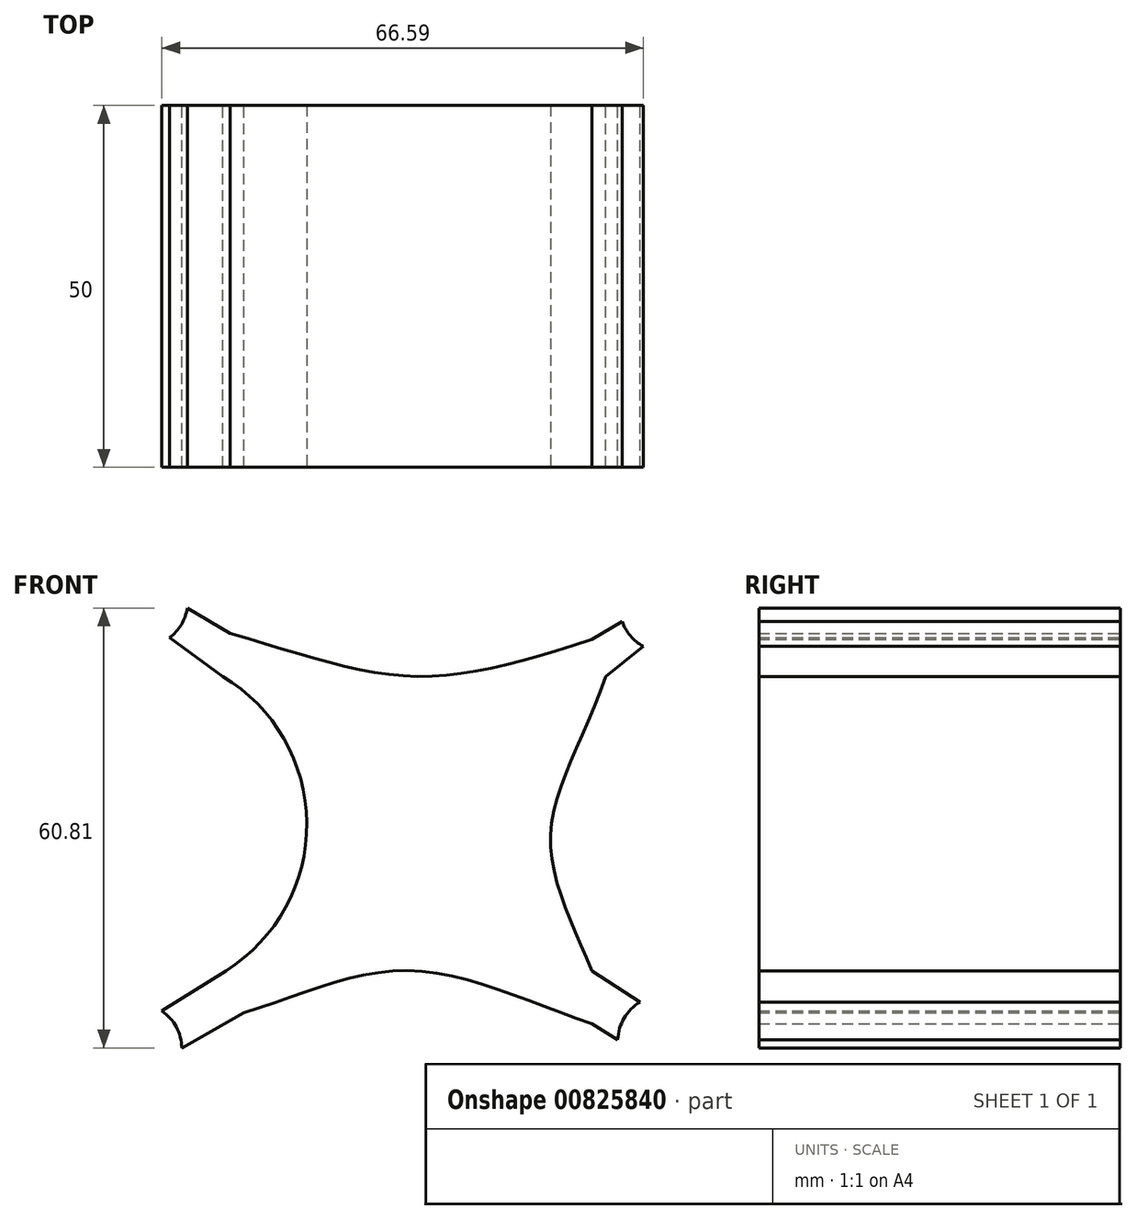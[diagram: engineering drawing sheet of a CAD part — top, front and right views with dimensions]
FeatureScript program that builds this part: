
annotation { "Feature Type Name" : "Feature", "Feature Type Description" : "" }
export const myFeature = defineFeature(function(context is Context, id is Id, definition is map)
    precondition{}
    {
        {
            var Q0;
            Q0=qCreatedBy(makeId("Front.planeOp"),FACE);
            var sketch = newSketch(context, id + "F0", { "sketchPlane" : qUnion([Q0])});
            skFitSpline(sketch, "E0", {"points": [v(-24.9, 27.81) * mm, v(0, 21.88) * mm, v(25.14, 27) * mm], "startDerivative": vector(57.8, -16.86) * mm, "endDerivative": vector(59.8, 19.27) * mm});
            skFitSpline(sketch, "E1", {"points": [v(-23.03, -24.68) * mm, v(0, -18.82) * mm, v(25.14, -26.2) * mm], "startDerivative": vector(50.66, 15.76) * mm, "endDerivative": vector(51.2, -17.15) * mm});
            skFitSpline(sketch, "E2", {"points": [v(-25.96, 21.84) * mm, v(-19.9, 0) * mm, v(-25.5, -18.86) * mm], "startDerivative": vector(18.38, -48.38) * mm, "endDerivative": vector(-20.64, -43.87) * mm});
            skFitSpline(sketch, "E3", {"points": [v(27, 21.84) * mm, v(19.4, 0) * mm, v(25.14, -18.86) * mm], "startDerivative": vector(-16.97, -49.86) * mm, "endDerivative": vector(17.53, -41.49) * mm});
            skCircle(sketch, "E4", {"center": v(35.05, -28.62) * mm, "radius": 6.35 * mm});
            skCircle(sketch, "E5", {"center": v(35.2, 31.51) * mm, "radius": 6.25 * mm});
            skLineSegment(sketch, "E6", {"start": v(-25.96, 21.84) * mm, "end": v(-35.41, 28.75) * mm});
            skLineSegment(sketch, "E7", {"start": v(-24.9, 27.81) * mm, "end": v(-32.52, 32.27) * mm});
            skLineSegment(sketch, "E8", {"start": v(25.14, -26.2) * mm, "end": v(32.16, -30.54) * mm});
            skLineSegment(sketch, "E9", {"start": v(35.81, -25.82) * mm, "end": v(25.14, -18.86) * mm});
            skLineSegment(sketch, "E10", {"start": v(-25.5, -18.86) * mm, "end": v(-37.2, -26.2) * mm});
            skLineSegment(sketch, "E11", {"start": v(-23.03, -24.68) * mm, "end": v(-33.22, -30.42) * mm});
            skCircle(sketch, "E12", {"center": v(-37.13, 32.27) * mm, "radius": 6.35 * mm});
            skCircle(sketch, "E13", {"center": v(-37.96, -29.66) * mm, "radius": 6.35 * mm});
            skLineSegment(sketch, "E14", {"start": v(25.14, 27) * mm, "end": v(29.31, 29.44) * mm});
            skLineSegment(sketch, "E15", {"start": v(27, 21.84) * mm, "end": v(32.22, 26.03) * mm});
            skSolve(sketch);
        }
        {
            var Q0;
            {var subQ1=sQuery(id+"F0.wireOp",EDGE,"E0");Q0=makeQuery(id+"F0.imprint","IMPRINT",FACE,{"disambiguationData":[TD([[makeQuery(id+"F0.imprint","IMPRINT",EDGE,{"derivedFrom":subQ1}),-1.0]])]});}
            extrude(context, id + "F1", {"entities" : qUnion([Q0]), "depth" : 50 * mm, "offsetDistance" : 25.4 * mm});
        }
        {
            var Q0;
            Q0=makeQuery(id+"F1.opExtrude","CAP_FACE",FACE,{"disambiguationData":[OSD([sQuery(id+"F0.wireOp",EDGE,"E0"),sQuery(id+"F0.wireOp",EDGE,"E1"),sQuery(id+"F0.wireOp",EDGE,"E2"),sQuery(id+"F0.wireOp",EDGE,"E3"),sQuery(id+"F0.wireOp",EDGE,"E4"),sQuery(id+"F0.wireOp",EDGE,"E5"),sQuery(id+"F0.wireOp",EDGE,"E6"),sQuery(id+"F0.wireOp",EDGE,"E7"),sQuery(id+"F0.wireOp",EDGE,"E8"),sQuery(id+"F0.wireOp",EDGE,"E9"),sQuery(id+"F0.wireOp",EDGE,"E10"),sQuery(id+"F0.wireOp",EDGE,"E11"),sQuery(id+"F0.wireOp",EDGE,"E12"),sQuery(id+"F0.wireOp",EDGE,"E13"),sQuery(id+"F0.wireOp",EDGE,"E14"),sQuery(id+"F0.wireOp",EDGE,"E15")])],"isStart":false});
            var sketch = newSketch(context, id + "F2", { "sketchPlane" : qUnion([Q0])});
            skArc(sketch, "E16", {"start": v(-25.5, -18.86) * mm, "mid": v(-14.32, 1.62) * mm, "end": v(-25.96, 21.84) * mm});
            skSolve(sketch);
        }
        {
            var Q0;
            Q0 = qSketchRegion(id + "F2", true);
            var Q1;
            Q1=makeQuery(id+"F2.imprint","IMPRINT",FACE,{"disambiguationData":[TD([[makeQuery(id+"F2.imprint","IMPRINT",EDGE,{"derivedFrom":sQuery(id+"F2.wireOp",EDGE,"E16")}),1.0]])]});
            extrude(context, id + "F3", {"entities" : qUnion([Q0, Q1]), "operationType" : NewBodyOperationType.REMOVE, "endBound" : BoundingType.THROUGH_ALL, "oppositeDirection" : true, "depth" : 25 * mm, "offsetDistance" : 25 * mm});
        }
        {
            var Q0;
            Q0=qCreatedBy(makeId("Front.planeOp"),FACE);
            var sketch = newSketch(context, id + "F4", { "sketchPlane" : qUnion([Q0])});
            skCircle(sketch, "E17", {"center": v(22.98, 0.85) * mm, "radius": 16.02 * mm});
            skPoint(sketch, "E17.first.point", {"position": v(25.21, 16.71) * mm});
            skPoint(sketch, "E17.second.point", {"position": v(23.65, -15.16) * mm});
            skPoint(sketch, "E17.third.point", {"position": v(7.8, -4.25) * mm});
            skSolve(sketch);
        }
        {
            var Q0;
            Q0=makeQuery(id+"F4.imprint","IMPRINT",FACE,{"disambiguationData":[TD([[makeQuery(id+"F4.imprint","IMPRINT",EDGE,{"derivedFrom":sQuery(id+"F4.wireOp",EDGE,"E17")}),1.0]])]});
            extrude(context, id + "F5", {"entities" : qUnion([Q0]), "operationType" : NewBodyOperationType.REMOVE, "oppositeDirection" : true, "depth" : 37.7 * mm, "offsetDistance" : 25 * mm});
        }
        {
            var Q0;
            Q0=qCreatedBy(makeId("Front.planeOp"),FACE);
            var sketch = newSketch(context, id + "F6", { "sketchPlane" : qUnion([Q0])});
            skCircle(sketch, "E18", {"center": v(-1.84, 21.17) * mm, "radius": 14 * mm});
            skPoint(sketch, "E18.first.point", {"position": v(10.91, 26.95) * mm});
            skPoint(sketch, "E18.second.point", {"position": v(-15.77, 22.65) * mm});
            skPoint(sketch, "E18.third.point", {"position": v(-15.02, 16.43) * mm});
            skSolve(sketch);
        }
        {
            var Q0;
            Q0=makeQuery(id+"F6.imprint","IMPRINT",FACE,{"disambiguationData":[TD([[makeQuery(id+"F6.imprint","IMPRINT",EDGE,{"derivedFrom":sQuery(id+"F6.wireOp",EDGE,"E18")}),1.0]])]});
            extrude(context, id + "F7", {"entities" : qUnion([Q0]), "operationType" : NewBodyOperationType.REMOVE, "oppositeDirection" : true, "depth" : 63 * mm, "offsetDistance" : 25 * mm});
        }
    });
